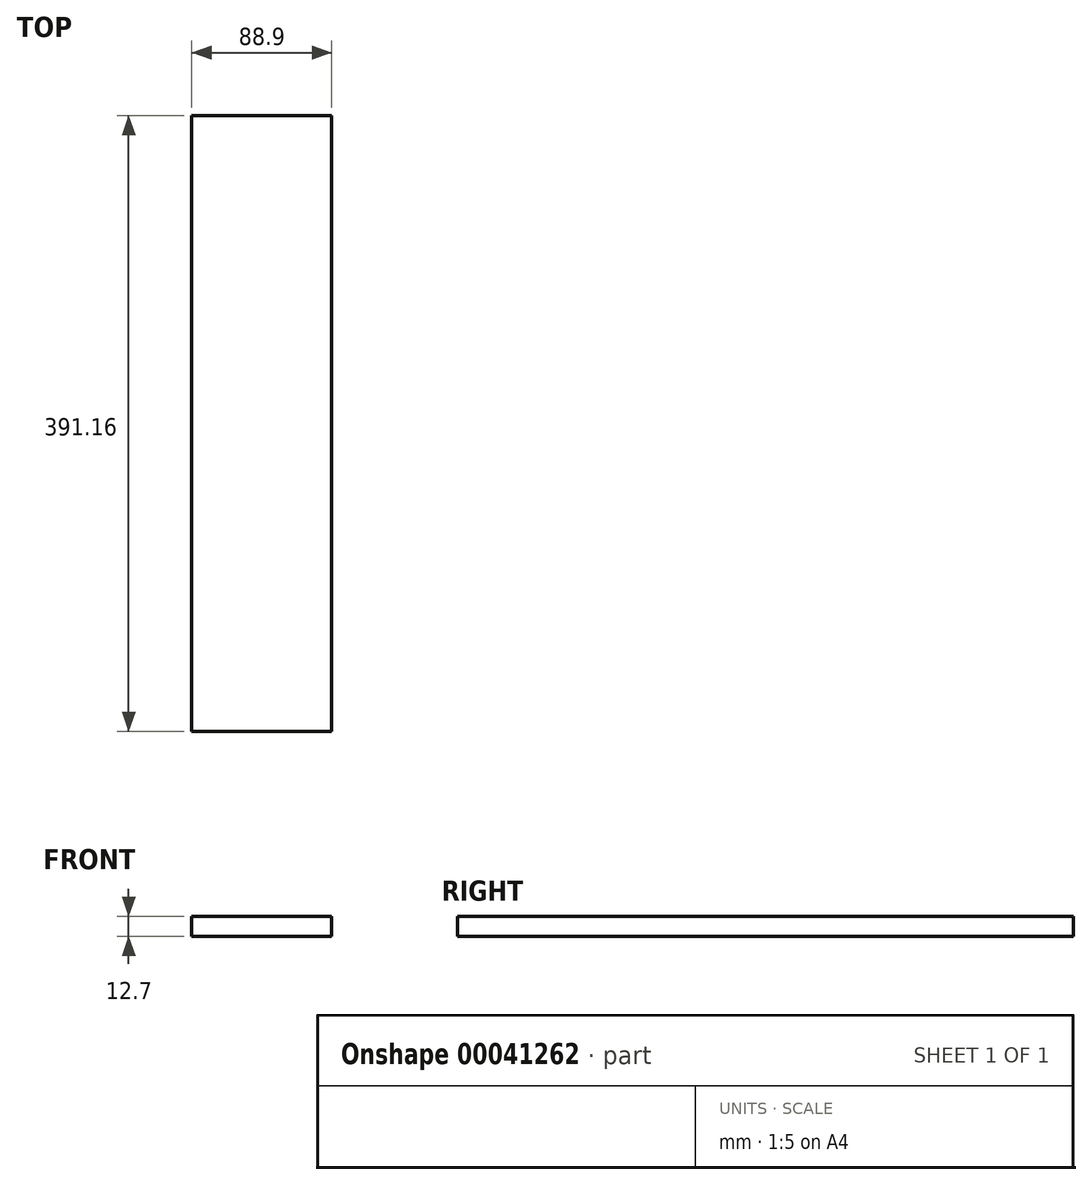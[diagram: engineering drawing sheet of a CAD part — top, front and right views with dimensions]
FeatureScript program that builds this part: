
annotation { "Feature Type Name" : "Feature", "Feature Type Description" : "" }
export const myFeature = defineFeature(function(context is Context, id is Id, definition is map)
    precondition{}
    {
        {
            var Q0;
            Q0=qCreatedBy(makeId("Front.planeOp"),FACE);
            var sketch = newSketch(context, id + "F0", { "sketchPlane" : qUnion([Q0])});
            skLineSegment(sketch, "E0.bottom", {"start": v(-44.45, 0) * mm, "end": v(44.45, 0) * mm});
            skLineSegment(sketch, "E0.top", {"start": v(-44.45, 12.7) * mm, "end": v(44.45, 12.7) * mm});
            skLineSegment(sketch, "E0.left", {"start": v(-44.45, 0) * mm, "end": v(-44.45, 12.7) * mm});
            skLineSegment(sketch, "E0.right", {"start": v(44.45, 0) * mm, "end": v(44.45, 12.7) * mm});
            skSolve(sketch);
        }
        {
            var Q0;
            Q0=makeQuery(id+"F0.imprint","IMPRINT",FACE,{"disambiguationData":[TD([[makeQuery(id+"F0.imprint","IMPRINT",EDGE,{"derivedFrom":sQuery(id+"F0.wireOp",EDGE,"E0.bottom")}),1.0]])]});
            extrude(context, id + "F1", {"entities" : qUnion([Q0]), "depth" : 391.16 * mm});
        }
    });
